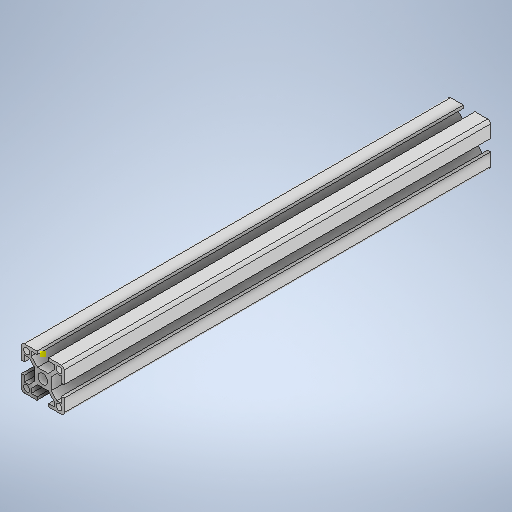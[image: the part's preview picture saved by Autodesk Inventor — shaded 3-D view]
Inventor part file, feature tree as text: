
AUTODESK INVENTOR PART (.ipt)
format: ipt  version: 2025 (Build 290162000, 162)  size: 311,296 bytes
history: native  units: in
note: dims shown in document units (in); Inventor stores cm internally (conversion verified against a paired STEP export)
features: sketch x2, extrude x1
ambient origin geometry x8: Origin, YZ Plane, XZ Plane, XY Plane, X Axis, Y Axis, Z Axis, Center Point
bodies: Solid1 (feature_tree)
feature tree (3):
  extrude  "Extrusion1"  Depth=11.811in
  sketch  "Sketch2"  dims[d9=0.0344in]
  sketch  "Sketch1"  dims[d6=11.811in d7=0.0in d8=0.1969in]
